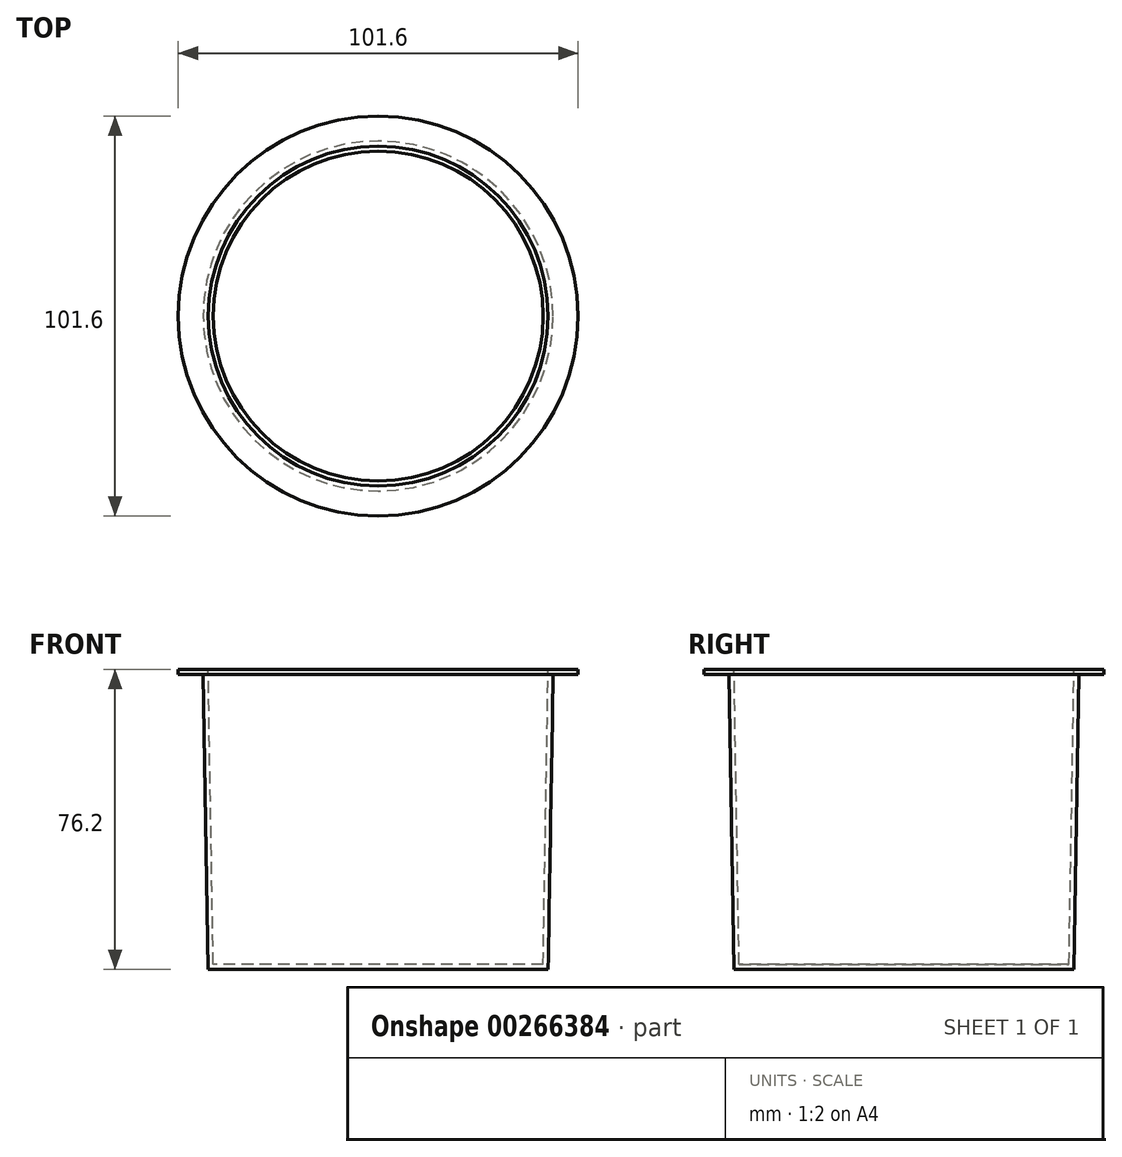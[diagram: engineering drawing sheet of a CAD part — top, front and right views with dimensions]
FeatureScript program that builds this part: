
annotation { "Feature Type Name" : "Feature", "Feature Type Description" : "" }
export const myFeature = defineFeature(function(context is Context, id is Id, definition is map)
    precondition{}
    {
        {
            var Q0;
            Q0=qCreatedBy(makeId("Front.planeOp"),FACE);
            var sketch = newSketch(context, id + "F0", { "sketchPlane" : qUnion([Q0])});
            skLineSegment(sketch, "E0", {"start": v(0, 0) * mm, "end": v(50.8, 0) * mm});
            skLineSegment(sketch, "E1", {"start": v(50.8, 0) * mm, "end": v(50.8, -1.27) * mm});
            skLineSegment(sketch, "E2", {"start": v(50.8, -1.27) * mm, "end": v(44.45, -1.27) * mm});
            skLineSegment(sketch, "E3", {"start": v(0, 0) * mm, "end": v(0, -76.2) * mm});
            skLineSegment(sketch, "E4", {"start": v(0, -76.2) * mm, "end": v(43.18, -76.2) * mm});
            skLineSegment(sketch, "E5", {"start": v(43.18, -76.2) * mm, "end": v(44.45, -1.27) * mm});
            skLineSegment(sketch, "E6", {"start": v(0, -76.2) * mm, "end": v(0, -74.93) * mm});
            skLineSegment(sketch, "E7", {"start": v(0, -74.93) * mm, "end": v(41.91, -74.93) * mm});
            skLineSegment(sketch, "E8", {"start": v(50.8, 0) * mm, "end": v(43.18, 0) * mm});
            skLineSegment(sketch, "E9", {"start": v(43.18, 0) * mm, "end": v(41.91, -74.93) * mm});
            skSolve(sketch);
        }
        {
            var Q0;
            Q0=makeQuery(id+"F0.imprint","IMPRINT",FACE,{"disambiguationData":[TD([[makeQuery(id+"F0.imprint","IMPRINT",EDGE,{"derivedFrom":sQuery(id+"F0.wireOp",EDGE,"E1")}),-1.0]])]});
            var Q1;
            Q1=sQuery(id+"F0.wireOp",EDGE,"E3");
            revolve(context, id + "F1", {"entities" : qUnion([Q0]), "axis" : qUnion([Q1]), "revolveType" : RevolveType.FULL});
        }
    });
